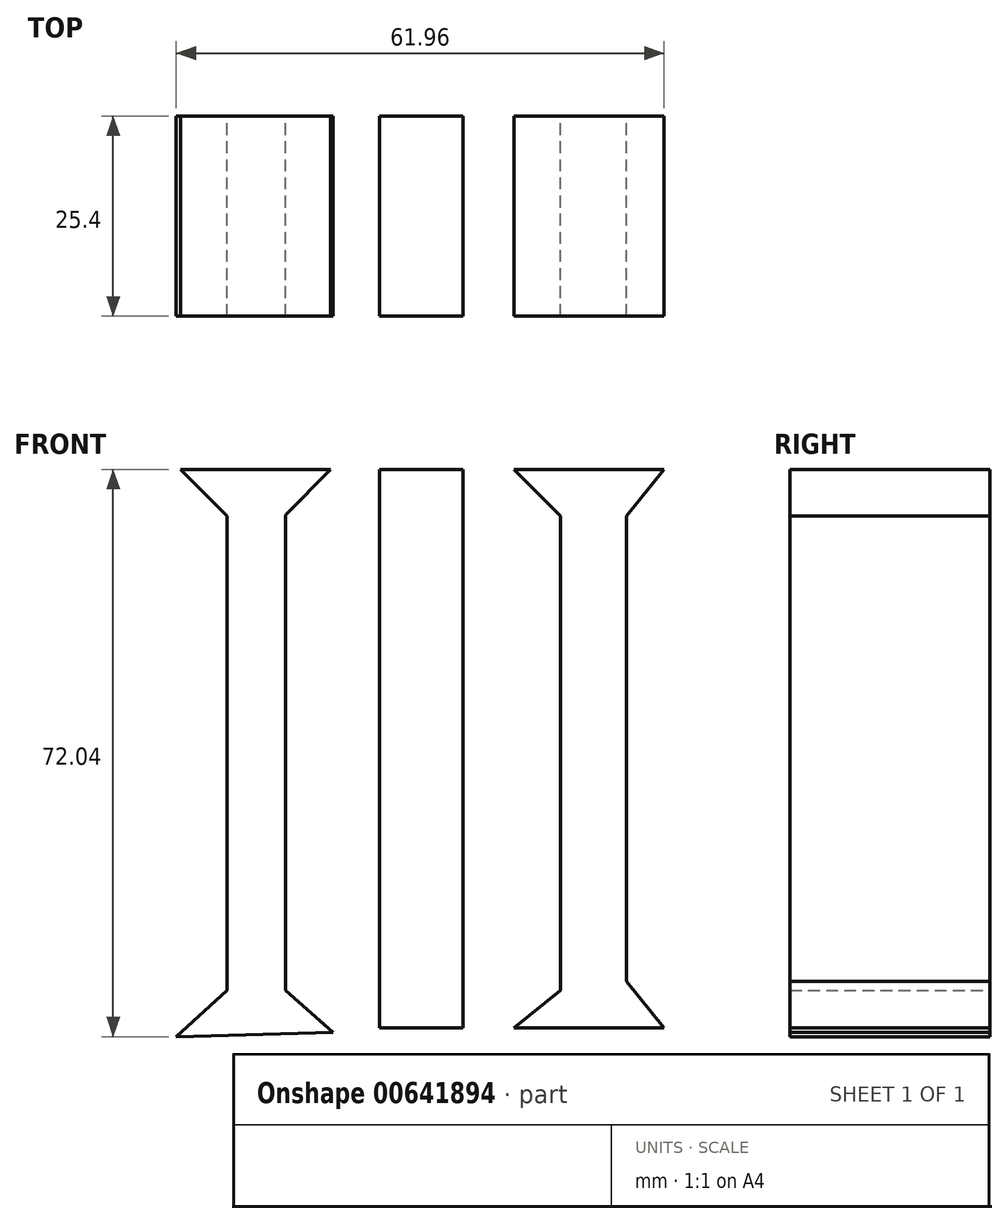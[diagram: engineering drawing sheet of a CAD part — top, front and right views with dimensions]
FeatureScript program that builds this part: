
annotation { "Feature Type Name" : "Feature", "Feature Type Description" : "" }
export const myFeature = defineFeature(function(context is Context, id is Id, definition is map)
    precondition{}
    {
        {
            var Q0;
            Q0=qCreatedBy(makeId("Front.planeOp"),FACE);
            var sketch = newSketch(context, id + "F0", { "sketchPlane" : qUnion([Q0])});
            skLineSegment(sketch, "E0", {"start": v(-63.94, 46.3) * mm, "end": v(-58.05, 40.42) * mm});
            skLineSegment(sketch, "E1", {"start": v(-58.05, 40.42) * mm, "end": v(-58.05, -19.85) * mm});
            skLineSegment(sketch, "E2", {"start": v(-58.05, -19.85) * mm, "end": v(-64.5, -25.74) * mm});
            skLineSegment(sketch, "E3", {"start": v(-63.94, 46.3) * mm, "end": v(-44.87, 46.3) * mm});
            skLineSegment(sketch, "E4", {"start": v(-44.87, 46.3) * mm, "end": v(-50.62, 40.56) * mm});
            skLineSegment(sketch, "E5", {"start": v(-50.62, 40.56) * mm, "end": v(-50.62, -19.85) * mm});
            skLineSegment(sketch, "E6", {"start": v(-50.62, -19.85) * mm, "end": v(-44.6, -25.18) * mm});
            skLineSegment(sketch, "E7", {"start": v(-64.5, -25.74) * mm, "end": v(-44.6, -25.18) * mm});
            skLineSegment(sketch, "E8", {"start": v(-38.7, 46.3) * mm, "end": v(-38.7, -24.62) * mm});
            skLineSegment(sketch, "E9", {"start": v(-38.7, 46.3) * mm, "end": v(-28.05, 46.3) * mm});
            skLineSegment(sketch, "E10", {"start": v(-28.05, 46.3) * mm, "end": v(-28.05, -24.62) * mm});
            skLineSegment(sketch, "E11", {"start": v(-28.05, -24.62) * mm, "end": v(-38.7, -24.62) * mm});
            skLineSegment(sketch, "E12", {"start": v(-21.6, 46.3) * mm, "end": v(-2.54, 46.3) * mm});
            skLineSegment(sketch, "E13", {"start": v(-21.6, 46.3) * mm, "end": v(-15.72, 40.42) * mm});
            skLineSegment(sketch, "E14", {"start": v(-2.54, 46.3) * mm, "end": v(-7.3, 40.42) * mm});
            skLineSegment(sketch, "E15", {"start": v(-15.72, -19.85) * mm, "end": v(-21.6, -24.62) * mm});
            skLineSegment(sketch, "E16", {"start": v(-7.3, -18.73) * mm, "end": v(-2.54, -24.62) * mm});
            skLineSegment(sketch, "E17", {"start": v(-15.72, -19.85) * mm, "end": v(-15.72, 40.42) * mm});
            skLineSegment(sketch, "E18", {"start": v(-7.3, 40.42) * mm, "end": v(-7.3, -18.73) * mm});
            skLineSegment(sketch, "E19", {"start": v(-21.6, -24.62) * mm, "end": v(-2.54, -24.62) * mm});
            skSolve(sketch);
        }
        {
            var Q0;
            Q0 = qSketchRegion(id + "F0", true);
            extrude(context, id + "F1", {"entities" : qUnion([Q0]), "depth" : 25.4 * mm, "offsetDistance" : 25.4 * mm});
        }
    });
